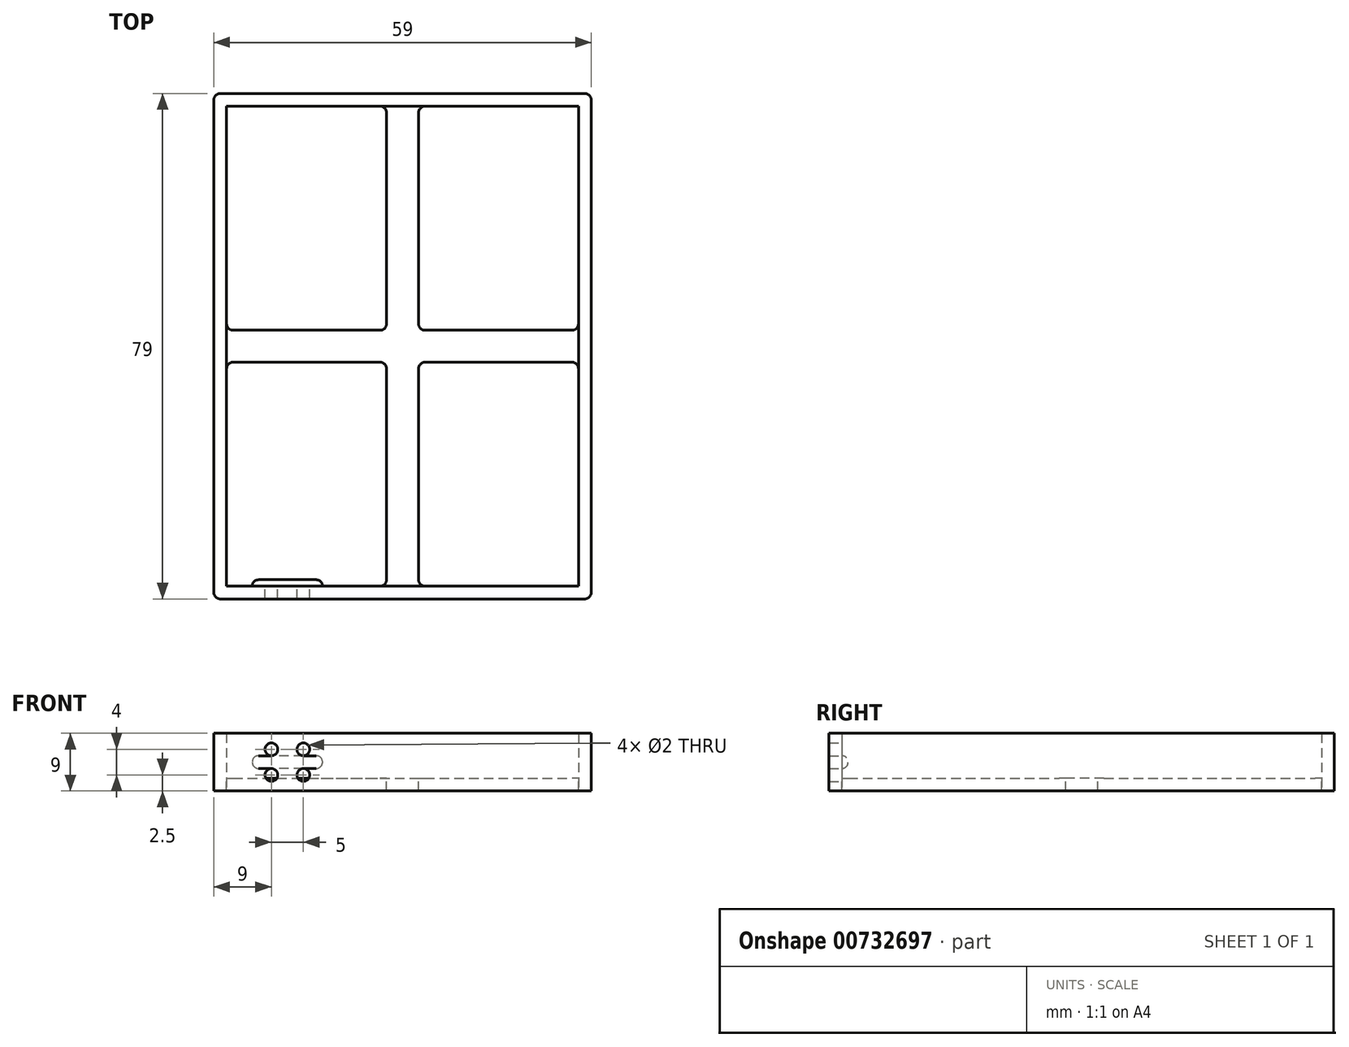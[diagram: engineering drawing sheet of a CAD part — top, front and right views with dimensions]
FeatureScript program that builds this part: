
annotation { "Feature Type Name" : "Feature", "Feature Type Description" : "" }
export const myFeature = defineFeature(function(context is Context, id is Id, definition is map)
    precondition{}
    {
        {
            var Q0;
            Q0=qCreatedBy(makeId("Top.planeOp"),FACE);
            var sketch = newSketch(context, id + "F0", { "sketchPlane" : qUnion([Q0])});
            skLineSegment(sketch, "E0.bottom", {"start": v(-27.5, 37.5) * mm, "end": v(27.5, 37.5) * mm});
            skLineSegment(sketch, "E0.top", {"start": v(-27.5, -37.5) * mm, "end": v(27.5, -37.5) * mm});
            skLineSegment(sketch, "E0.left", {"start": v(-27.5, 37.5) * mm, "end": v(-27.5, -37.5) * mm});
            skLineSegment(sketch, "E0.right", {"start": v(27.5, 37.5) * mm, "end": v(27.5, -37.5) * mm});
            skPoint(sketch, "E0.middle", {"position": v(0, 0) * mm});
            skLineSegment(sketch, "E1.0", {"start": v(-29.5, 39.5) * mm, "end": v(29.5, 39.5) * mm});
            skLineSegment(sketch, "E1.1", {"start": v(-29.5, 39.5) * mm, "end": v(-29.5, -39.5) * mm});
            skLineSegment(sketch, "E1.2", {"start": v(-29.5, -39.5) * mm, "end": v(29.5, -39.5) * mm});
            skLineSegment(sketch, "E1.3", {"start": v(29.5, 39.5) * mm, "end": v(29.5, -39.5) * mm});
            skPoint(sketch, "E2.trimOffspring.end.orphan", {"position": v(-1.5, 37.5) * mm});
            skPoint(sketch, "E3.start.orphan", {"position": v(-27.5, 1.5) * mm});
            skPoint(sketch, "E4.trimOffspring.end.orphan", {"position": v(1.5, 37.5) * mm});
            skPoint(sketch, "E5.trimOffspring.end.orphan", {"position": v(27.5, 1.5) * mm});
            skPoint(sketch, "E6.trimOffspring.end.orphan", {"position": v(27.5, -1.5) * mm});
            skPoint(sketch, "E7.start.orphan", {"position": v(2.5, -37.5) * mm});
            skPoint(sketch, "E8.MirrorCS.start.orphan", {"position": v(-2.5, -37.5) * mm});
            skPoint(sketch, "E9.MirrorCS.start.orphan", {"position": v(-27.5, -1.5) * mm});
            skSolve(sketch);
        }
        {
            var Q0;
            Q0=makeQuery(id+"F0.imprint","IMPRINT",FACE,{"disambiguationData":[TD([[makeQuery(id+"F0.imprint","IMPRINT",EDGE,{"derivedFrom":sQuery(id+"F0.wireOp",EDGE,"E1.0")}),-1.0]])]});
            extrude(context, id + "F1", {"entities" : qUnion([Q0]), "depth" : 9 * mm, "offsetDistance" : 25 * mm});
        }
        {
            var Q0;
            Q0=qCreatedBy(makeId("Top.planeOp"),FACE);
            var sketch = newSketch(context, id + "F2", { "sketchPlane" : qUnion([Q0])});
            skLineSegment(sketch, "E10.bottom", {"start": v(-2.5, 38.5) * mm, "end": v(2.5, 38.5) * mm});
            skLineSegment(sketch, "E10.top", {"start": v(-2.5, -38.5) * mm, "end": v(2.5, -38.5) * mm});
            skLineSegment(sketch, "E10.left", {"start": v(-28.5, 2.5) * mm, "end": v(-28.5, -2.5) * mm});
            skLineSegment(sketch, "E10.right", {"start": v(28.5, 2.5) * mm, "end": v(28.5, -2.5) * mm});
            skPoint(sketch, "E10.middle", {"position": v(0, 0) * mm});
            skLineSegment(sketch, "E11", {"start": v(2.5, -38.5) * mm, "end": v(2.5, -2.5) * mm});
            skLineSegment(sketch, "E12.MirrorCS", {"start": v(-2.5, -38.5) * mm, "end": v(-2.5, -2.5) * mm});
            skLineSegment(sketch, "E13", {"start": v(-28.5, 2.5) * mm, "end": v(-2.5, 2.5) * mm});
            skLineSegment(sketch, "E14.MirrorCS", {"start": v(-28.5, -2.5) * mm, "end": v(-2.5, -2.5) * mm});
            skLineSegment(sketch, "E15.trimOffspring", {"start": v(2.5, 2.5) * mm, "end": v(28.5, 2.5) * mm});
            skLineSegment(sketch, "E16.trimOffspring", {"start": v(2.5, 2.5) * mm, "end": v(2.5, 38.5) * mm});
            skLineSegment(sketch, "E17.trimOffspring", {"start": v(2.5, -2.5) * mm, "end": v(28.5, -2.5) * mm});
            skLineSegment(sketch, "E18.trimOffspring", {"start": v(-2.5, 2.5) * mm, "end": v(-2.5, 38.5) * mm});
            skPoint(sketch, "E19.orphan", {"position": v(-28.5, 38.5) * mm});
            skPoint(sketch, "E20.orphan", {"position": v(28.5, 38.5) * mm});
            skPoint(sketch, "E21.orphan", {"position": v(28.5, -38.5) * mm});
            skPoint(sketch, "E22.orphan", {"position": v(-28.5, -38.5) * mm});
            skSolve(sketch);
        }
        {
            var Q0;
            Q0 = qSketchRegion(id + "F2", true);
            extrude(context, id + "F3", {"entities" : qUnion([Q0]), "operationType" : NewBodyOperationType.ADD, "depth" : 2 * mm, "offsetDistance" : 25 * mm});
        }
        {
            var Q0;
            Q0=makeQuery(id+"F1.opExtrude","SWEPT_FACE",FACE,{"disambiguationData":[OSD([sQuery(id+"F0.wireOp",EDGE,"E0.top")])]});
            var sketch = newSketch(context, id + "F4", { "sketchPlane" : qUnion([Q0])});
            skCircle(sketch, "E23", {"center": v(20.5, 2.5) * mm, "radius": 1 * mm});
            skPoint(sketch, "E24", {"position": v(21.5, 4.29) * mm});
            skLineSegment(sketch, "E25.left", {"start": v(27.5, 2.5) * mm, "end": v(27.5, 2.5) * mm});
            skPoint(sketch, "E25.middle", {"position": v(19.5, 2.5) * mm});
            skCircle(sketch, "E26.0.1.0", {"center": v(20.5, 6.5) * mm, "radius": 1 * mm});
            skCircle(sketch, "E26.1.0.0", {"center": v(15.5, 2.5) * mm, "radius": 1 * mm});
            skCircle(sketch, "E26.1.1.0", {"center": v(15.5, 6.5) * mm, "radius": 1 * mm});
            skLineSegment(sketch, "E26.direction1", {"start": v(21.5, 4.29) * mm, "end": v(16.5, 4.29) * mm, "construction": true});
            skLineSegment(sketch, "E26.direction2", {"start": v(21.5, 4.29) * mm, "end": v(21.5, 7.29) * mm, "construction": true});
            skLineSegment(sketch, "E27", {"start": v(27.5, 0) * mm, "end": v(27.5, 2.5) * mm});
            skSolve(sketch);
        }
        {
            var Q0;
            Q0 = qSketchRegion(id + "F4", true);
            extrude(context, id + "F5", {"entities" : qUnion([Q0]), "operationType" : NewBodyOperationType.REMOVE, "endBound" : BoundingType.THROUGH_ALL, "oppositeDirection" : true, "depth" : 25 * mm, "offsetDistance" : 25 * mm});
        }
        {
            var Q0;
            Q0=makeQuery(id+"F1.opExtrude","SWEPT_EDGE",EDGE,{"disambiguationData":[OSD([sQuery(id+"F0.wireOp",EDGE,"E1.1"),sQuery(id+"F0.wireOp",EDGE,"E1.2")])]});
            var Q1;
            Q1=makeQuery(id+"F1.opExtrude","SWEPT_EDGE",EDGE,{"disambiguationData":[OSD([sQuery(id+"F0.wireOp",EDGE,"E1.2"),sQuery(id+"F0.wireOp",EDGE,"E1.3")])]});
            var Q2;
            Q2=makeQuery(id+"F1.opExtrude","SWEPT_EDGE",EDGE,{"disambiguationData":[OSD([sQuery(id+"F0.wireOp",EDGE,"E1.0"),sQuery(id+"F0.wireOp",EDGE,"E1.1")])]});
            var Q3;
            Q3=makeQuery(id+"F1.opExtrude","SWEPT_EDGE",EDGE,{"disambiguationData":[OSD([sQuery(id+"F0.wireOp",EDGE,"E1.0"),sQuery(id+"F0.wireOp",EDGE,"E1.3")])]});
            var Q4;
            Q4=makeQuery(id+"F3.opExtrude","SWEPT_EDGE",EDGE,{"disambiguationData":[OSD([sQuery(id+"F2.wireOp",EDGE,"E13"),sQuery(id+"F2.wireOp",EDGE,"E18.trimOffspring")])]});
            var Q5;
            Q5=makeQuery(id+"F3.opExtrude","SWEPT_EDGE",EDGE,{"disambiguationData":[OSD([sQuery(id+"F2.wireOp",EDGE,"E15.trimOffspring"),sQuery(id+"F2.wireOp",EDGE,"E16.trimOffspring")])]});
            var Q6;
            Q6=makeQuery(id+"F3.opExtrude","SWEPT_EDGE",EDGE,{"disambiguationData":[OSD([sQuery(id+"F2.wireOp",EDGE,"E11"),sQuery(id+"F2.wireOp",EDGE,"E17.trimOffspring")])]});
            var Q7;
            Q7=makeQuery(id+"F3.opExtrude","SWEPT_EDGE",EDGE,{"disambiguationData":[OSD([sQuery(id+"F2.wireOp",EDGE,"E12.MirrorCS"),sQuery(id+"F2.wireOp",EDGE,"E14.MirrorCS")])]});
            var Q8;
            Q8=makeQuery(id+"F3.opExtrude","SWEPT_EDGE",EDGE,{"disambiguationData":[OSD([sQuery(id+"F2.wireOp",EDGE,"E10.right"),sQuery(id+"F2.wireOp",EDGE,"E17.trimOffspring")])]});
            var Q9;
            Q9=makeQuery(id+"F3.opExtrude","SWEPT_EDGE",EDGE,{"disambiguationData":[OSD([sQuery(id+"F2.wireOp",EDGE,"E10.right"),sQuery(id+"F2.wireOp",EDGE,"E15.trimOffspring")])]});
            var Q10;
            Q10=makeQuery(id+"F3.opExtrude","SWEPT_EDGE",EDGE,{"disambiguationData":[OSD([sQuery(id+"F2.wireOp",EDGE,"E10.top"),sQuery(id+"F2.wireOp",EDGE,"E12.MirrorCS")])]});
            var Q11;
            Q11=makeQuery(id+"F3.opExtrude","SWEPT_EDGE",EDGE,{"disambiguationData":[OSD([sQuery(id+"F2.wireOp",EDGE,"E10.bottom"),sQuery(id+"F2.wireOp",EDGE,"E18.trimOffspring")])]});
            var Q12;
            Q12=makeQuery(id+"F3.opExtrude","SWEPT_EDGE",EDGE,{"disambiguationData":[OSD([sQuery(id+"F2.wireOp",EDGE,"E10.top"),sQuery(id+"F2.wireOp",EDGE,"E11")])]});
            var Q13;
            Q13=makeQuery(id+"F3.opExtrude","SWEPT_EDGE",EDGE,{"disambiguationData":[OSD([sQuery(id+"F2.wireOp",EDGE,"E10.left"),sQuery(id+"F2.wireOp",EDGE,"E13")])]});
            var Q14;
            Q14=makeQuery(id+"F3.opExtrude","SWEPT_EDGE",EDGE,{"disambiguationData":[OSD([sQuery(id+"F2.wireOp",EDGE,"E10.bottom"),sQuery(id+"F2.wireOp",EDGE,"E16.trimOffspring")])]});
            var Q15;
            Q15=makeQuery(id+"F3.opExtrude","SWEPT_EDGE",EDGE,{"disambiguationData":[OSD([sQuery(id+"F2.wireOp",EDGE,"E10.left"),sQuery(id+"F2.wireOp",EDGE,"E14.MirrorCS")])]});
            fillet(context, id + "F6", {"entities" : qUnion([Q0, Q1, Q2, Q3, Q4, Q5, Q6, Q7, Q8, Q9, Q10, Q11, Q12, Q13, Q14, Q15]), "radius" : 1 * mm, "tangentPropagation" : true, "allowEdgeOverflow" : false});
        }
        {
            var Q0;
            Q0=makeQuery(id+"F1.opExtrude","SWEPT_FACE",FACE,{"disambiguationData":[OSD([sQuery(id+"F0.wireOp",EDGE,"E0.left")])]});
            cPlane(context, id + "F7", {"entities" : qUnion([Q0]), "cplaneType" : CPlaneType.OFFSET, "offset" : 4 * mm, "width" : 150 * mm, "height" : 150 * mm});
        }
        {
            var Q0;
            Q0=qCreatedBy(id+"F7.planeOp",FACE);
            var sketch = newSketch(context, id + "F8", { "sketchPlane" : qUnion([Q0])});
            skLineSegment(sketch, "E28.0", {"start": v(-37.5, 5.5) * mm, "end": v(-37.5, 3.5) * mm});
            skPoint(sketch, "E29", {"position": v(-36.5, 4.5) * mm});
            skPoint(sketch, "E30", {"position": v(-40.14, 4.5) * mm});
            skArc(sketch, "E31", {"start": v(-37.5, 3.5) * mm, "mid": v(-36.5, 4.5) * mm, "end": v(-37.5, 5.5) * mm});
            skPoint(sketch, "E32.0.start.orphan", {"position": v(-37.5, 7.5) * mm});
            skPoint(sketch, "E33.orphan", {"position": v(-37.5, 9) * mm});
            skPoint(sketch, "E34.0.end.orphan", {"position": v(-37.5, 1.5) * mm});
            skPoint(sketch, "E35.orphan", {"position": v(-37.5, 0) * mm});
            skSolve(sketch);
        }
        {
            var Q0;
            Q0=makeQuery(id+"F8.imprint","IMPRINT",FACE,{"disambiguationData":[TD([[makeQuery(id+"F8.imprint","IMPRINT",EDGE,{"derivedFrom":sQuery(id+"F8.wireOp",EDGE,"E28.0")}),1.0]])]});
            extrude(context, id + "F9", {"entities" : qUnion([Q0]), "depth" : 11 * mm, "offsetDistance" : 25 * mm});
        }
        {
            var Q0;
            Q0=makeQuery(id+"F9.opExtrude","CAP_EDGE",EDGE,{"disambiguationData":[OSD([sQuery(id+"F8.wireOp",EDGE,"E31")])],"isStart":true});
            var Q1;
            Q1=makeQuery(id+"F9.opExtrude","CAP_EDGE",EDGE,{"disambiguationData":[OSD([sQuery(id+"F8.wireOp",EDGE,"E31")])],"isStart":false});
            fillet(context, id + "F10", {"entities" : qUnion([Q0, Q1]), "radius" : 1 * mm, "tangentPropagation" : true, "allowEdgeOverflow" : false});
        }
        {
            var Q0;
            Q0=makeQuery(id+"F3.boolean.opBoolean","INTERSECT",EDGE,{"derivedFrom":[makeQuery(id+"F1.opExtrude","SWEPT_FACE",FACE,{"disambiguationData":[OSD([sQuery(id+"F0.wireOp",EDGE,"E0.top")])]}),makeQuery(id+"F3.opExtrude","SWEPT_FACE",FACE,{"disambiguationData":[OSD([sQuery(id+"F2.wireOp",EDGE,"E12.MirrorCS")])]})]});
            var Q1;
            Q1=makeQuery(id+"F3.boolean.opBoolean","INTERSECT",EDGE,{"derivedFrom":[makeQuery(id+"F1.opExtrude","SWEPT_FACE",FACE,{"disambiguationData":[OSD([sQuery(id+"F0.wireOp",EDGE,"E0.top")])]}),makeQuery(id+"F3.opExtrude","SWEPT_FACE",FACE,{"disambiguationData":[OSD([sQuery(id+"F2.wireOp",EDGE,"E11")])]})]});
            var Q2;
            Q2=makeQuery(id+"F3.boolean.opBoolean","INTERSECT",EDGE,{"derivedFrom":[makeQuery(id+"F1.opExtrude","SWEPT_FACE",FACE,{"disambiguationData":[OSD([sQuery(id+"F0.wireOp",EDGE,"E0.right")])]}),makeQuery(id+"F3.opExtrude","SWEPT_FACE",FACE,{"disambiguationData":[OSD([sQuery(id+"F2.wireOp",EDGE,"E15.trimOffspring")])]})]});
            var Q3;
            Q3=makeQuery(id+"F3.boolean.opBoolean","INTERSECT",EDGE,{"derivedFrom":[makeQuery(id+"F1.opExtrude","SWEPT_FACE",FACE,{"disambiguationData":[OSD([sQuery(id+"F0.wireOp",EDGE,"E0.right")])]}),makeQuery(id+"F3.opExtrude","SWEPT_FACE",FACE,{"disambiguationData":[OSD([sQuery(id+"F2.wireOp",EDGE,"E17.trimOffspring")])]})]});
            var Q4;
            Q4=makeQuery(id+"F3.boolean.opBoolean","INTERSECT",EDGE,{"derivedFrom":[makeQuery(id+"F1.opExtrude","SWEPT_FACE",FACE,{"disambiguationData":[OSD([sQuery(id+"F0.wireOp",EDGE,"E0.bottom")])]}),makeQuery(id+"F3.opExtrude","SWEPT_FACE",FACE,{"disambiguationData":[OSD([sQuery(id+"F2.wireOp",EDGE,"E18.trimOffspring")])]})]});
            var Q5;
            Q5=makeQuery(id+"F3.boolean.opBoolean","INTERSECT",EDGE,{"derivedFrom":[makeQuery(id+"F1.opExtrude","SWEPT_FACE",FACE,{"disambiguationData":[OSD([sQuery(id+"F0.wireOp",EDGE,"E0.bottom")])]}),makeQuery(id+"F3.opExtrude","SWEPT_FACE",FACE,{"disambiguationData":[OSD([sQuery(id+"F2.wireOp",EDGE,"E16.trimOffspring")])]})]});
            var Q6;
            Q6=makeQuery(id+"F3.boolean.opBoolean","INTERSECT",EDGE,{"derivedFrom":[makeQuery(id+"F1.opExtrude","SWEPT_FACE",FACE,{"disambiguationData":[OSD([sQuery(id+"F0.wireOp",EDGE,"E0.left")])]}),makeQuery(id+"F3.opExtrude","SWEPT_FACE",FACE,{"disambiguationData":[OSD([sQuery(id+"F2.wireOp",EDGE,"E14.MirrorCS")])]})]});
            var Q7;
            Q7=makeQuery(id+"F3.boolean.opBoolean","INTERSECT",EDGE,{"derivedFrom":[makeQuery(id+"F1.opExtrude","SWEPT_FACE",FACE,{"disambiguationData":[OSD([sQuery(id+"F0.wireOp",EDGE,"E0.left")])]}),makeQuery(id+"F3.opExtrude","SWEPT_FACE",FACE,{"disambiguationData":[OSD([sQuery(id+"F2.wireOp",EDGE,"E13")])]})]});
            fillet(context, id + "F11", {"entities" : qUnion([Q0, Q1, Q2, Q3, Q4, Q5, Q6, Q7]), "radius" : 1 * mm, "tangentPropagation" : true, "allowEdgeOverflow" : false});
        }
    });
